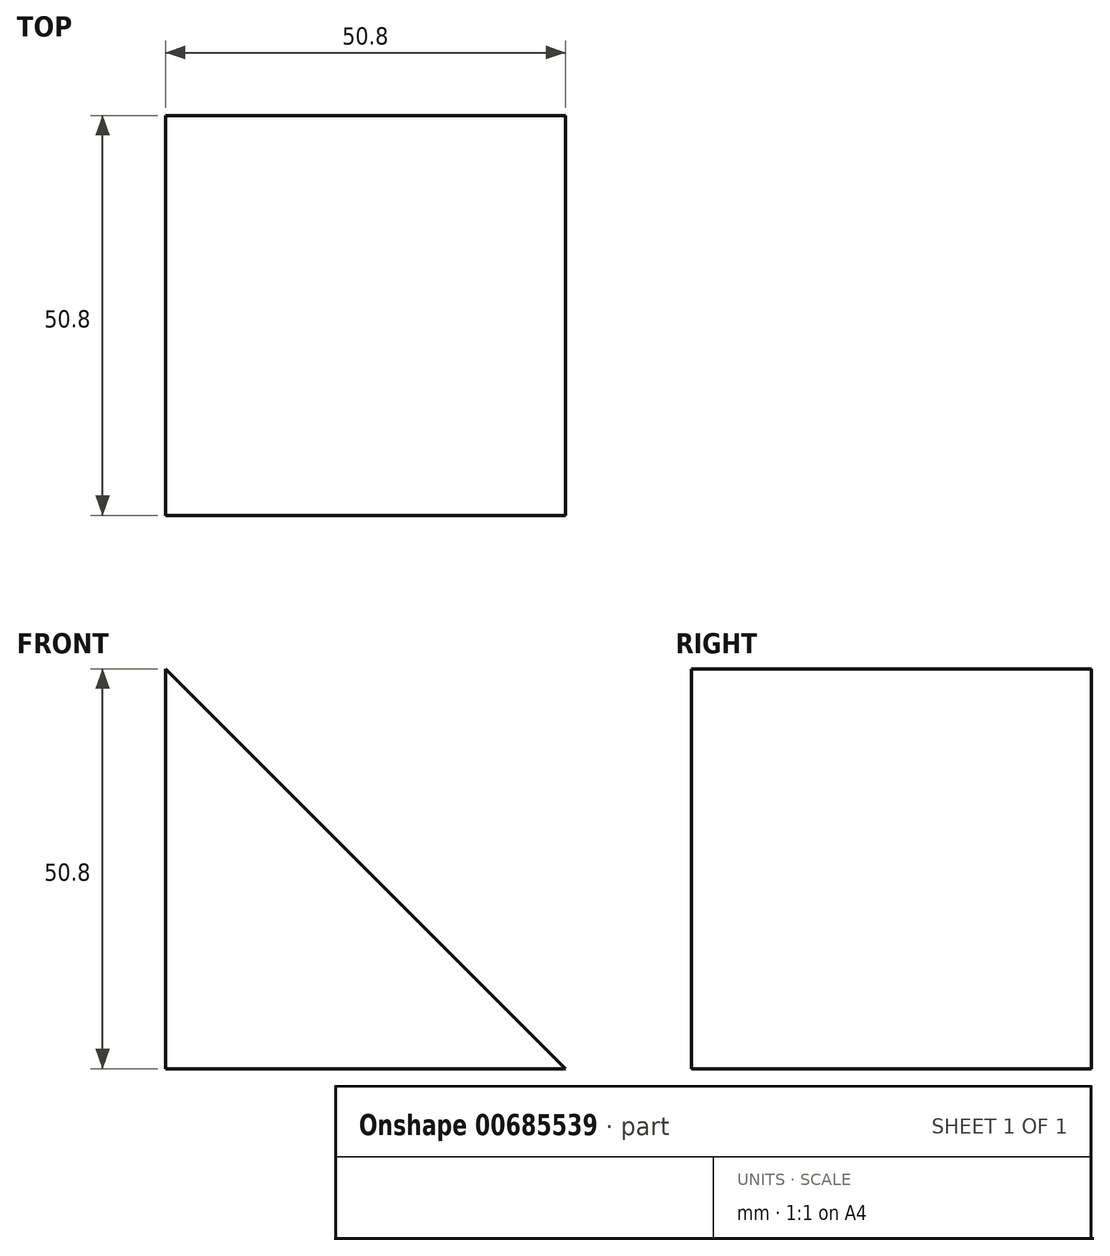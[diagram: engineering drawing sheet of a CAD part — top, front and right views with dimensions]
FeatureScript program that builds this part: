
annotation { "Feature Type Name" : "Feature", "Feature Type Description" : "" }
export const myFeature = defineFeature(function(context is Context, id is Id, definition is map)
    precondition{}
    {
        {
            var Q0;
            Q0=qCreatedBy(makeId("Front.planeOp"),FACE);
            var sketch = newSketch(context, id + "F0", { "sketchPlane" : qUnion([Q0])});
            skLineSegment(sketch, "E0", {"start": v(0, 0) * mm, "end": v(-50.8, 0) * mm});
            skLineSegment(sketch, "E1", {"start": v(-50.8, 0) * mm, "end": v(-50.8, 50.8) * mm});
            skLineSegment(sketch, "E2", {"start": v(-50.8, 50.8) * mm, "end": v(0, 0) * mm});
            skSolve(sketch);
        }
        {
            var Q0;
            Q0=makeQuery(id+"F0.imprint","IMPRINT",FACE,{"disambiguationData":[TD([[makeQuery(id+"F0.imprint","IMPRINT",EDGE,{"derivedFrom":sQuery(id+"F0.wireOp",EDGE,"E0")}),-1.0]])]});
            extrude(context, id + "F1", {"entities" : qUnion([Q0]), "depth" : 50.8 * mm, "offsetDistance" : 25.4 * mm});
        }
    });
